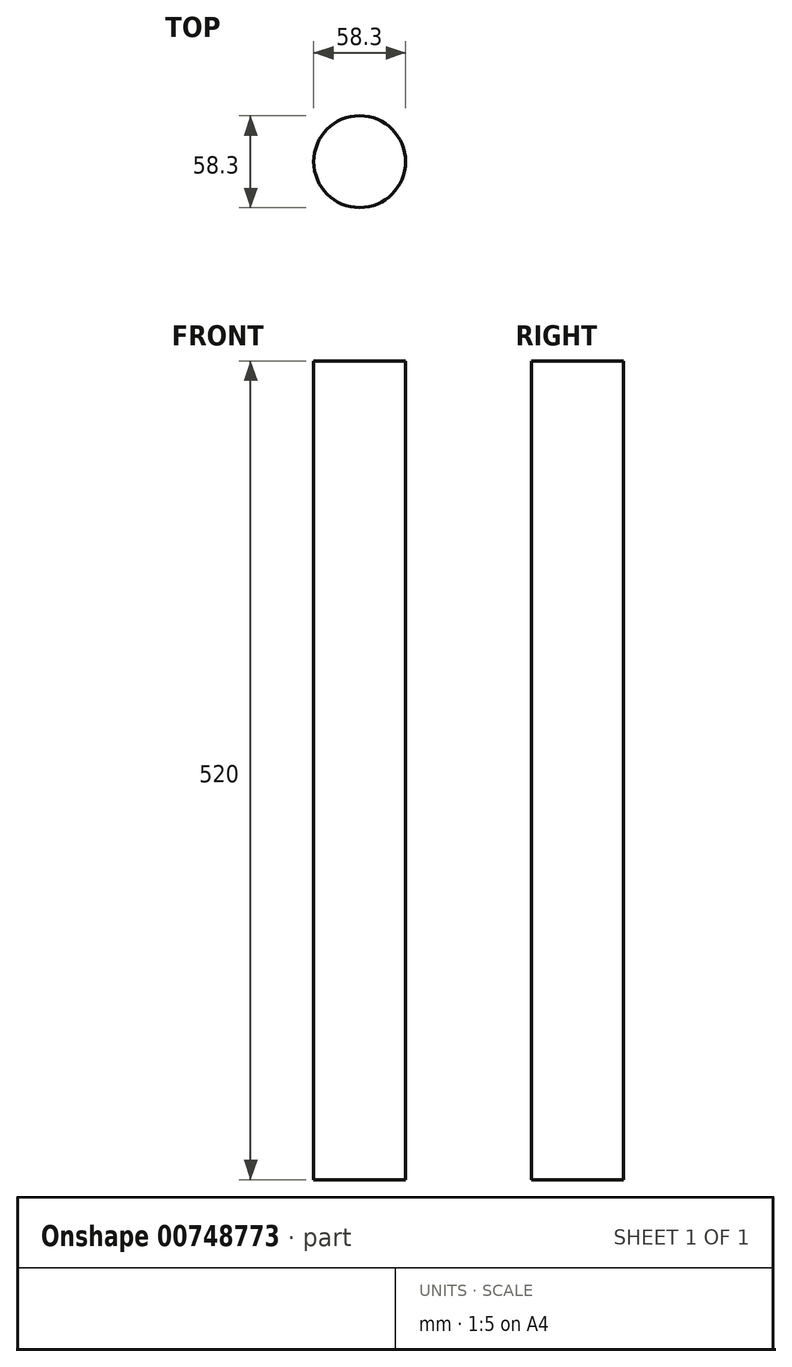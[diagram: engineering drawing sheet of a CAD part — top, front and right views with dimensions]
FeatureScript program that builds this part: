
annotation { "Feature Type Name" : "Feature", "Feature Type Description" : "" }
export const myFeature = defineFeature(function(context is Context, id is Id, definition is map)
    precondition{}
    {
        {
            var Q0;
            Q0=qCreatedBy(makeId("Top.planeOp"),FACE);
            var sketch = newSketch(context, id + "F0", { "sketchPlane" : qUnion([Q0])});
            skCircle(sketch, "E0", {"center": v(0, 0) * mm, "radius": 29.15 * mm});
            skSolve(sketch);
        }
        {
            var Q0;
            Q0 = qConstructionFilter(qBodyType(qCreatedBy(id + "F0" ,EDGE), BodyType.WIRE), ConstructionObject.NO);
            extrude(context, id + "F1", {"bodyType" : ToolBodyType.SURFACE, "surfaceEntities" : qUnion([Q0]), "depth" : 520 * mm, "offsetDistance" : 25 * mm});
        }
    });
